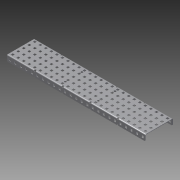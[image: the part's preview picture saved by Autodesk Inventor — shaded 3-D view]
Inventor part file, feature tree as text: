
AUTODESK INVENTOR PART (.ipt)
format: ipt  version: 2012 (Build 160160000, 160)  size: 1,924,096 bytes
history: native  units: in
note: dims shown in document units (in); Inventor stores cm internally (conversion verified against a paired STEP export)
features: other x1, imported_body x1, hole x1, sketch x1
ambient origin geometry x8: Origin, YZ Plane, XZ Plane, XY Plane, X Axis, Y Axis, Z Axis, Center Point
feature tree (4):
  parser-record x1  (decoder bookkeeping rows leaked as tree rows — omitted from the tree; the rows remain in map.json)
  imported_body  "Base1"
  hole  "Hole2"  [1 undecoded]
  sketch  "Sketch2"  dims[d8=0.182in d9=0.182in d10=0.182in d11=0.182in d12=0.182in d13=0.75in d14=0.375in d15=0.25in d16=0.5635in d17=1.0in d18=0.8108in]
note: 1 required parameter value undecoded (feature->parameter linkage not recoverable at this tier; creation-order binding heuristic only, values carry confidence <= 0.55)
